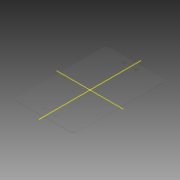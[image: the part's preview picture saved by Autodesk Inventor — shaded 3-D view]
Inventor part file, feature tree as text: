
AUTODESK INVENTOR PART (.ipt)
format: ipt  version: 2015 (Build 190159000, 159)  size: 137,728 bytes
history: native  units: mm
features: extrude x2, fillet x1, hole x1
ambient origin geometry x8: Origin, YZ Plane, XZ Plane, XY Plane, X Axis, Y Axis, Z Axis, Center Point
bodies: Solid1 (feature_tree)
feature tree (4):
  extrude  "Extrusión1"  Depth=243.0mm
  fillet  "Empalme2"  Radius=374.0mm
  hole  "Agujero1"  [1 undecoded]
  extrude  "Extrusión2"  TaperAngle=45.0deg  [1 undecoded]
note: 2 required parameter values undecoded (feature->parameter linkage not recoverable at this tier; creation-order binding heuristic only, values carry confidence <= 0.55)
